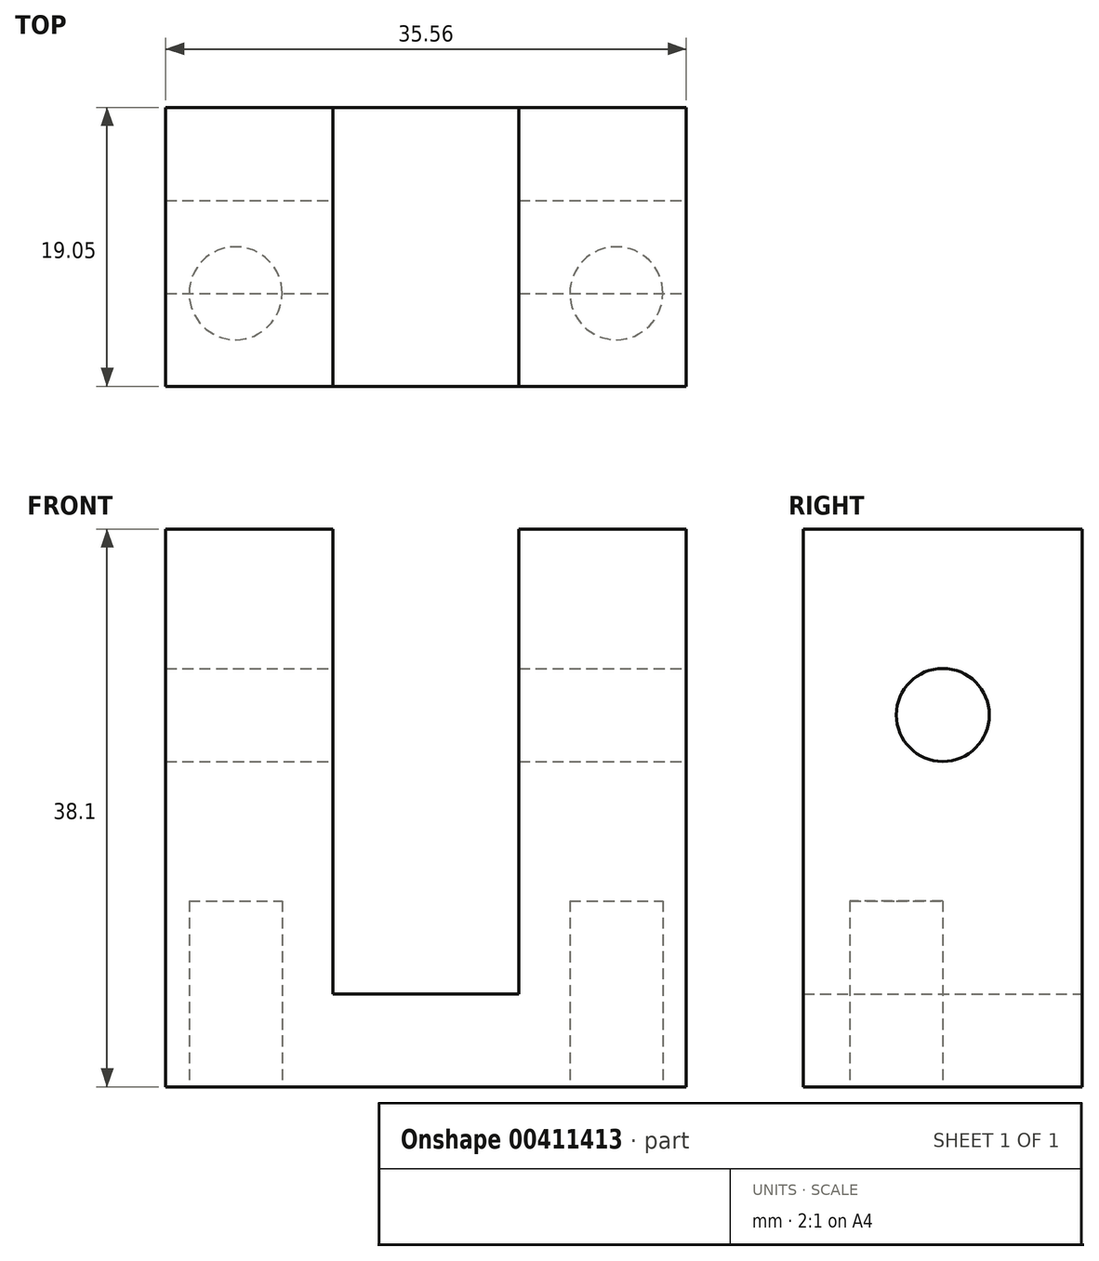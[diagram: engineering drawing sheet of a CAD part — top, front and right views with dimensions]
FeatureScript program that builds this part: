
annotation { "Feature Type Name" : "Feature", "Feature Type Description" : "" }
export const myFeature = defineFeature(function(context is Context, id is Id, definition is map)
    precondition{}
    {
        {
            var Q0;
            Q0=qCreatedBy(makeId("Front.planeOp"),FACE);
            var sketch = newSketch(context, id + "F0", { "sketchPlane" : qUnion([Q0])});
            skLineSegment(sketch, "E0.bottom", {"start": v(-17.78, 38.1) * mm, "end": v(-6.35, 38.1) * mm});
            skLineSegment(sketch, "E0.top", {"start": v(-17.78, 0) * mm, "end": v(-6.35, 0) * mm});
            skLineSegment(sketch, "E0.left", {"start": v(-17.78, 38.1) * mm, "end": v(-17.78, 0) * mm});
            skLineSegment(sketch, "E0.right", {"start": v(-6.35, 38.1) * mm, "end": v(-6.35, 6.35) * mm});
            skLineSegment(sketch, "E1.bottom", {"start": v(-17.78, 0) * mm, "end": v(17.78, 0) * mm});
            skLineSegment(sketch, "E1.top", {"start": v(-6.35, 6.35) * mm, "end": v(6.35, 6.35) * mm});
            skLineSegment(sketch, "E1.left", {"start": v(-17.78, 0) * mm, "end": v(-17.78, 6.35) * mm});
            skLineSegment(sketch, "E1.right", {"start": v(17.78, 0) * mm, "end": v(17.78, 6.35) * mm});
            skLineSegment(sketch, "E2.bottom", {"start": v(17.78, 0) * mm, "end": v(6.35, 0) * mm});
            skLineSegment(sketch, "E2.top", {"start": v(17.78, 38.1) * mm, "end": v(6.35, 38.1) * mm});
            skLineSegment(sketch, "E2.left", {"start": v(17.78, 0) * mm, "end": v(17.78, 38.1) * mm});
            skLineSegment(sketch, "E2.right", {"start": v(6.35, 6.35) * mm, "end": v(6.35, 38.1) * mm});
            skSolve(sketch);
        }
        {
            var Q0;
            Q0 = qSketchRegion(id + "F0", true);
            extrude(context, id + "F1", {"entities" : qUnion([Q0]), "depth" : 19.05 * mm});
        }
        {
            var Q0;
            Q0=makeQuery(id+"F1.opExtrude","SWEPT_FACE",FACE,{"disambiguationData":[OSD([sQuery(id+"F0.wireOp",EDGE,"E2.left")])]});
            var sketch = newSketch(context, id + "F2", { "sketchPlane" : qUnion([Q0])});
            skCircle(sketch, "E3", {"center": v(-9.53, 25.4) * mm, "radius": 3.17 * mm});
            skSolve(sketch);
        }
        {
            var Q0;
            Q0 = qSketchRegion(id + "F2", true);
            extrude(context, id + "F3", {"entities" : qUnion([Q0]), "operationType" : NewBodyOperationType.REMOVE, "oppositeDirection" : true, "depth" : 127 * mm});
        }
        {
            var Q0;
            Q0=makeQuery(id+"F1.opExtrude","SWEPT_FACE",FACE,{"disambiguationData":[OSD([sQuery(id+"F0.wireOp",EDGE,"E1.bottom"),sQuery(id+"F0.wireOp",EDGE,"E2.bottom")])]});
            var sketch = newSketch(context, id + "F4", { "sketchPlane" : qUnion([Q0])});
            skCircle(sketch, "E4", {"center": v(-13, 12.7) * mm, "radius": 3.18 * mm});
            skCircle(sketch, "E5", {"center": v(13, 12.7) * mm, "radius": 3.18 * mm});
            skSolve(sketch);
        }
        {
            var Q0;
            Q0 = qSketchRegion(id + "F4", true);
            extrude(context, id + "F5", {"entities" : qUnion([Q0]), "operationType" : NewBodyOperationType.REMOVE, "oppositeDirection" : true, "depth" : 12.7 * mm});
        }
    });
